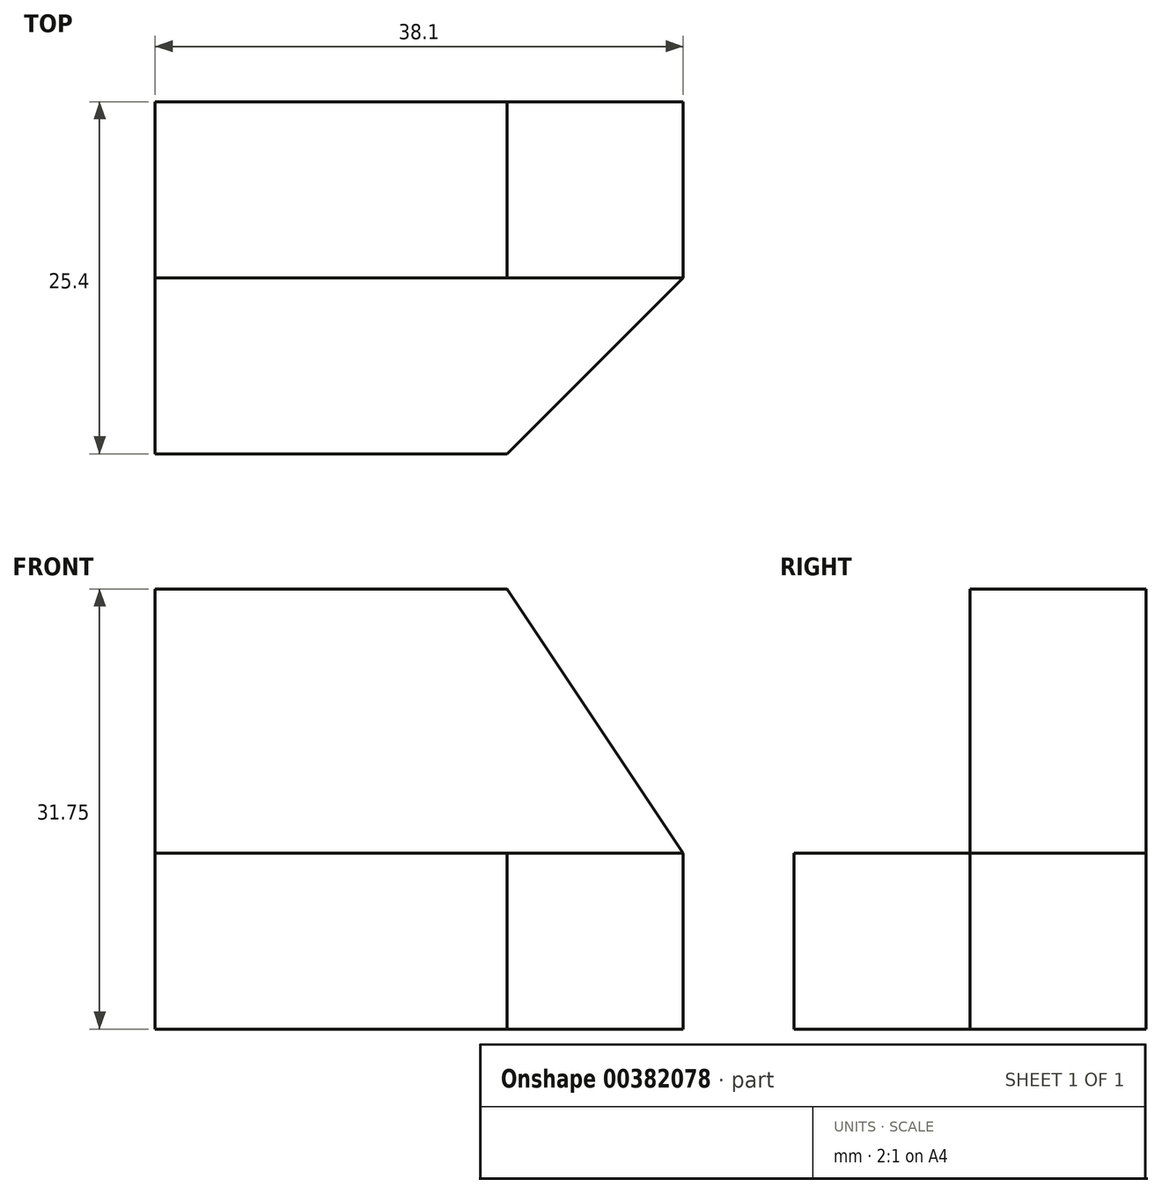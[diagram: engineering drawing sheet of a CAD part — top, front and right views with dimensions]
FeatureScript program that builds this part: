
annotation { "Feature Type Name" : "Feature", "Feature Type Description" : "" }
export const myFeature = defineFeature(function(context is Context, id is Id, definition is map)
    precondition{}
    {
        {
            var Q0;
            Q0=qCreatedBy(makeId("Right.planeOp"),FACE);
            var sketch = newSketch(context, id + "F0", { "sketchPlane" : qUnion([Q0])});
            skLineSegment(sketch, "E0", {"start": v(0, 0) * mm, "end": v(-25.4, 0) * mm});
            skLineSegment(sketch, "E1", {"start": v(-25.4, 0) * mm, "end": v(-25.4, 12.7) * mm});
            skLineSegment(sketch, "E2", {"start": v(-25.4, 12.7) * mm, "end": v(-12.7, 12.7) * mm});
            skLineSegment(sketch, "E3", {"start": v(-12.7, 12.7) * mm, "end": v(-12.7, 31.75) * mm});
            skLineSegment(sketch, "E4", {"start": v(-12.7, 31.75) * mm, "end": v(0, 31.75) * mm});
            skLineSegment(sketch, "E5", {"start": v(0, 31.75) * mm, "end": v(0, 0) * mm});
            skSolve(sketch);
        }
        {
            var Q0;
            Q0 = qSketchRegion(id + "F0", true);
            extrude(context, id + "F1", {"entities" : qUnion([Q0]), "depth" : 38.1 * mm});
        }
        {
            var Q0;
            Q0=makeQuery(id+"F1.opExtrude","SWEPT_FACE",FACE,{"disambiguationData":[OSD([sQuery(id+"F0.wireOp",EDGE,"E3")])]});
            var sketch = newSketch(context, id + "F2", { "sketchPlane" : qUnion([Q0])});
            skLineSegment(sketch, "E6", {"start": v(0, 31.75) * mm, "end": v(25.4, 31.75) * mm});
            skLineSegment(sketch, "E7", {"start": v(25.4, 31.75) * mm, "end": v(38.1, 12.7) * mm});
            skSolve(sketch);
        }
        {
            var Q0;
            Q0 = qSketchRegion(id + "F2", true);
            var Q1;
            {var subQ0=sQuery(id+"F2.wireOp",EDGE,"E7");Q1=makeQuery(id+"F2.imprint","IMPRINT",FACE,{"disambiguationData":[TD([[makeQuery(id+"F2.imprint","IMPRINT",EDGE,{"derivedFrom":subQ0}),1.0]])]});}
            extrude(context, id + "F3", {"entities" : qUnion([Q0, Q1]), "operationType" : NewBodyOperationType.REMOVE, "oppositeDirection" : true, "depth" : 25.4 * mm});
        }
        {
            var Q0;
            Q0=makeQuery(id+"F1.opExtrude","SWEPT_FACE",FACE,{"disambiguationData":[OSD([sQuery(id+"F0.wireOp",EDGE,"E2")])]});
            var sketch = newSketch(context, id + "F4", { "sketchPlane" : qUnion([Q0])});
            skLineSegment(sketch, "E8", {"start": v(0, -25.4) * mm, "end": v(25.4, -25.4) * mm});
            skLineSegment(sketch, "E9", {"start": v(25.4, -25.4) * mm, "end": v(38.1, -12.7) * mm});
            skSolve(sketch);
        }
        {
            var Q0;
            Q0 = qSketchRegion(id + "F4", true);
            var Q1;
            {var subQ0=sQuery(id+"F4.wireOp",EDGE,"E9");Q1=makeQuery(id+"F4.imprint","IMPRINT",FACE,{"disambiguationData":[TD([[makeQuery(id+"F4.imprint","IMPRINT",EDGE,{"derivedFrom":subQ0}),-1.0]])]});}
            extrude(context, id + "F5", {"entities" : qUnion([Q0, Q1]), "operationType" : NewBodyOperationType.REMOVE, "oppositeDirection" : true, "depth" : 25.4 * mm});
        }
    });
